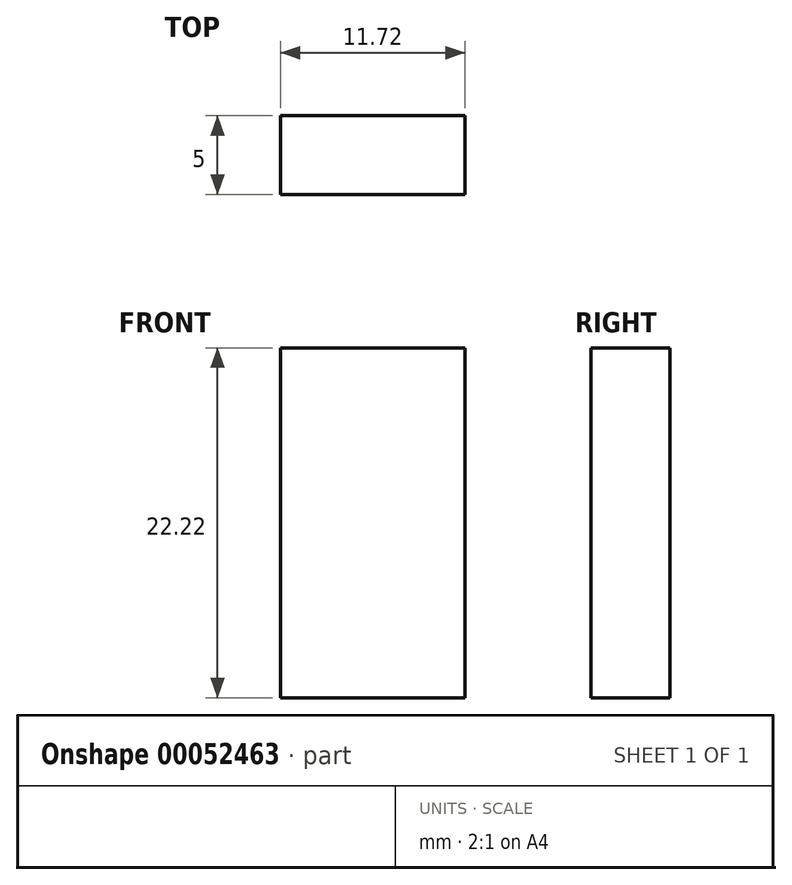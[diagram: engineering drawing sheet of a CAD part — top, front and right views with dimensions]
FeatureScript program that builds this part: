
annotation { "Feature Type Name" : "Feature", "Feature Type Description" : "" }
export const myFeature = defineFeature(function(context is Context, id is Id, definition is map)
    precondition{}
    {
        {
            var Q0;
            Q0=qCreatedBy(makeId("Front.planeOp"),FACE);
            var sketch = newSketch(context, id + "F0", { "sketchPlane" : qUnion([Q0])});
            skLineSegment(sketch, "E0", {"start": v(0, 33.52) * mm, "end": v(0, -43.62) * mm, "construction": true});
            skLineSegment(sketch, "E1", {"start": v(46.64, 0) * mm, "end": v(-41.8, 0) * mm, "construction": true});
            skLineSegment(sketch, "E2.bottom", {"start": v(-5.86, -11.1) * mm, "end": v(5.86, -11.1) * mm});
            skLineSegment(sketch, "E2.top", {"start": v(-5.86, 11.1) * mm, "end": v(5.86, 11.1) * mm});
            skLineSegment(sketch, "E2.left", {"start": v(-5.86, -11.1) * mm, "end": v(-5.86, 11.1) * mm});
            skLineSegment(sketch, "E2.right", {"start": v(5.86, -11.1) * mm, "end": v(5.86, 11.1) * mm});
            skPoint(sketch, "E2.middle", {"position": v(0, 0) * mm});
            skSolve(sketch);
        }
        {
            var Q0;
            Q0 = qSketchRegion(id + "F0", true);
            extrude(context, id + "F1", {"entities" : qUnion([Q0]), "depth" : 5 * mm});
        }
    });
